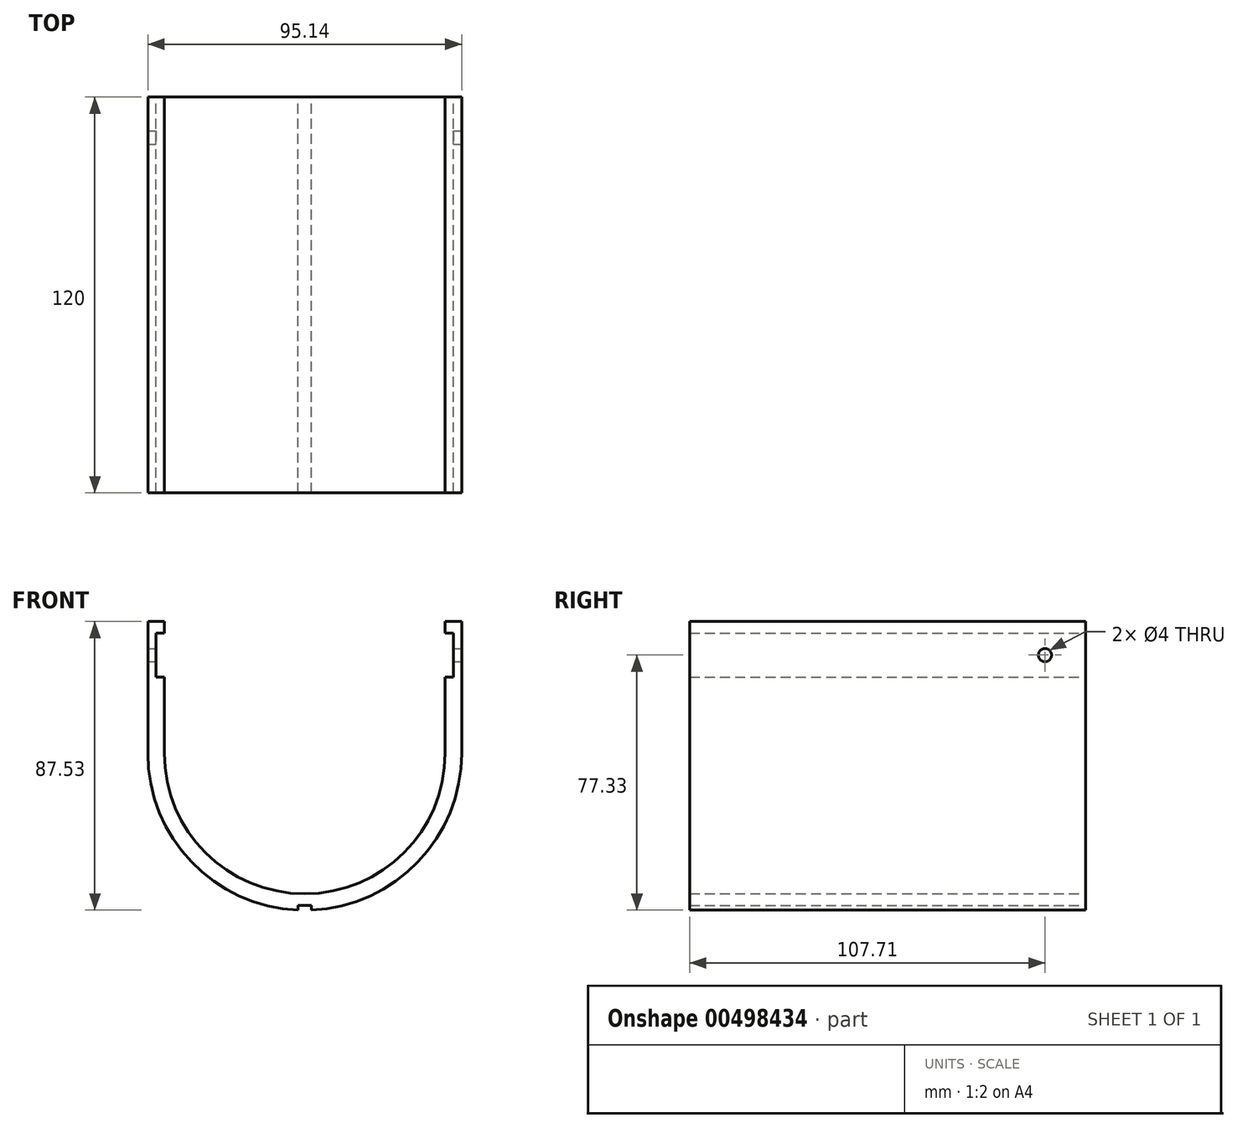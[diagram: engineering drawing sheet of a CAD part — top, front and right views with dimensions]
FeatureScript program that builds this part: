
annotation { "Feature Type Name" : "Feature", "Feature Type Description" : "" }
export const myFeature = defineFeature(function(context is Context, id is Id, definition is map)
    precondition{}
    {
        {
            var Q0;
            Q0=qCreatedBy(makeId("Front.planeOp"),FACE);
            var sketch = newSketch(context, id + "F0", { "sketchPlane" : qUnion([Q0])});
            skLineSegment(sketch, "E0.0", {"start": v(-47.57, 0) * mm, "end": v(-47.57, -40) * mm});
            skLineSegment(sketch, "E1.0", {"start": v(47.57, 0) * mm, "end": v(47.57, -40) * mm});
            skArc(sketch, "E2.0", {"start": v(-47.57, -40) * mm, "mid": v(-34.34, -72.92) * mm, "end": v(-2, -87.53) * mm});
            skLineSegment(sketch, "E3", {"start": v(-47.57, 0) * mm, "end": v(-42.57, 0) * mm});
            skLineSegment(sketch, "E4", {"start": v(42.57, 0) * mm, "end": v(47.57, 0) * mm});
            skLineSegment(sketch, "E5.bottom", {"start": v(-45.07, -3.5) * mm, "end": v(-42.57, -3.5) * mm});
            skLineSegment(sketch, "E5.top", {"start": v(-45.07, -16.9) * mm, "end": v(-42.57, -16.9) * mm});
            skLineSegment(sketch, "E5.left", {"start": v(-45.07, -3.5) * mm, "end": v(-45.07, -16.9) * mm});
            skLineSegment(sketch, "E6.MirrorCS", {"start": v(45.07, -3.5) * mm, "end": v(45.07, -16.9) * mm});
            skLineSegment(sketch, "E7.MirrorCS", {"start": v(45.07, -3.5) * mm, "end": v(42.57, -3.5) * mm});
            skLineSegment(sketch, "E8.MirrorCS", {"start": v(45.07, -16.9) * mm, "end": v(42.57, -16.9) * mm});
            skLineSegment(sketch, "E9.0", {"start": v(-42.57, 0) * mm, "end": v(-42.57, -3.5) * mm});
            skArc(sketch, "E10.0", {"start": v(-42.57, -40) * mm, "mid": v(0, -82.57) * mm, "end": v(42.57, -40) * mm});
            skLineSegment(sketch, "E11.0", {"start": v(42.57, 0) * mm, "end": v(42.57, -3.5) * mm});
            skPoint(sketch, "E12.0.end.orphan", {"position": v(40.07, -3.5) * mm});
            skPoint(sketch, "E13.orphan", {"position": v(40.07, -16.9) * mm});
            skLineSegment(sketch, "E14.trimOffspring", {"start": v(42.57, -16.9) * mm, "end": v(42.57, -40) * mm});
            skLineSegment(sketch, "E15.trimOffspring", {"start": v(-42.57, -16.9) * mm, "end": v(-42.57, -40) * mm});
            skPoint(sketch, "E16.0.end.orphan", {"position": v(-40.07, -3.5) * mm});
            skPoint(sketch, "E17.orphan", {"position": v(-40.07, -16.9) * mm});
            skLineSegment(sketch, "E18", {"start": v(-2, -87.53) * mm, "end": v(-2, -86.03) * mm});
            skLineSegment(sketch, "E19.MirrorCS", {"start": v(2, -87.53) * mm, "end": v(2, -86.03) * mm});
            skArc(sketch, "E20.0", {"start": v(-2, -86.03) * mm, "mid": v(0, -86.07) * mm, "end": v(2, -86.03) * mm});
            skArc(sketch, "E21.trimOffspring", {"start": v(2, -87.53) * mm, "mid": v(34.34, -72.92) * mm, "end": v(47.57, -40) * mm});
            skSolve(sketch);
        }
        {
            var Q0;
            Q0 = qSketchRegion(id + "F0", true);
            extrude(context, id + "F1", {"entities" : qUnion([Q0]), "depth" : 120 * mm});
        }
        {
            var Q0;
            Q0=makeQuery(id+"F1.opExtrude","SWEPT_FACE",FACE,{"disambiguationData":[OSD([sQuery(id+"F0.wireOp",EDGE,"E1.0")])]});
            var sketch = newSketch(context, id + "F2", { "sketchPlane" : qUnion([Q0])});
            skLineSegment(sketch, "E22.0", {"start": v(0, -16.9) * mm, "end": v(-120, -16.9) * mm, "construction": true});
            skCircle(sketch, "E23", {"center": v(-12.29, -10.2) * mm, "radius": 2 * mm});
            skLineSegment(sketch, "E24.0", {"start": v(-120, -3.5) * mm, "end": v(0, -3.5) * mm, "construction": true});
            skSolve(sketch);
        }
        {
            var Q0;
            Q0 = qSketchRegion(id + "F2", true);
            extrude(context, id + "F3", {"entities" : qUnion([Q0]), "operationType" : NewBodyOperationType.REMOVE, "endBound" : BoundingType.THROUGH_ALL, "oppositeDirection" : true, "depth" : 25 * mm});
        }
    });
